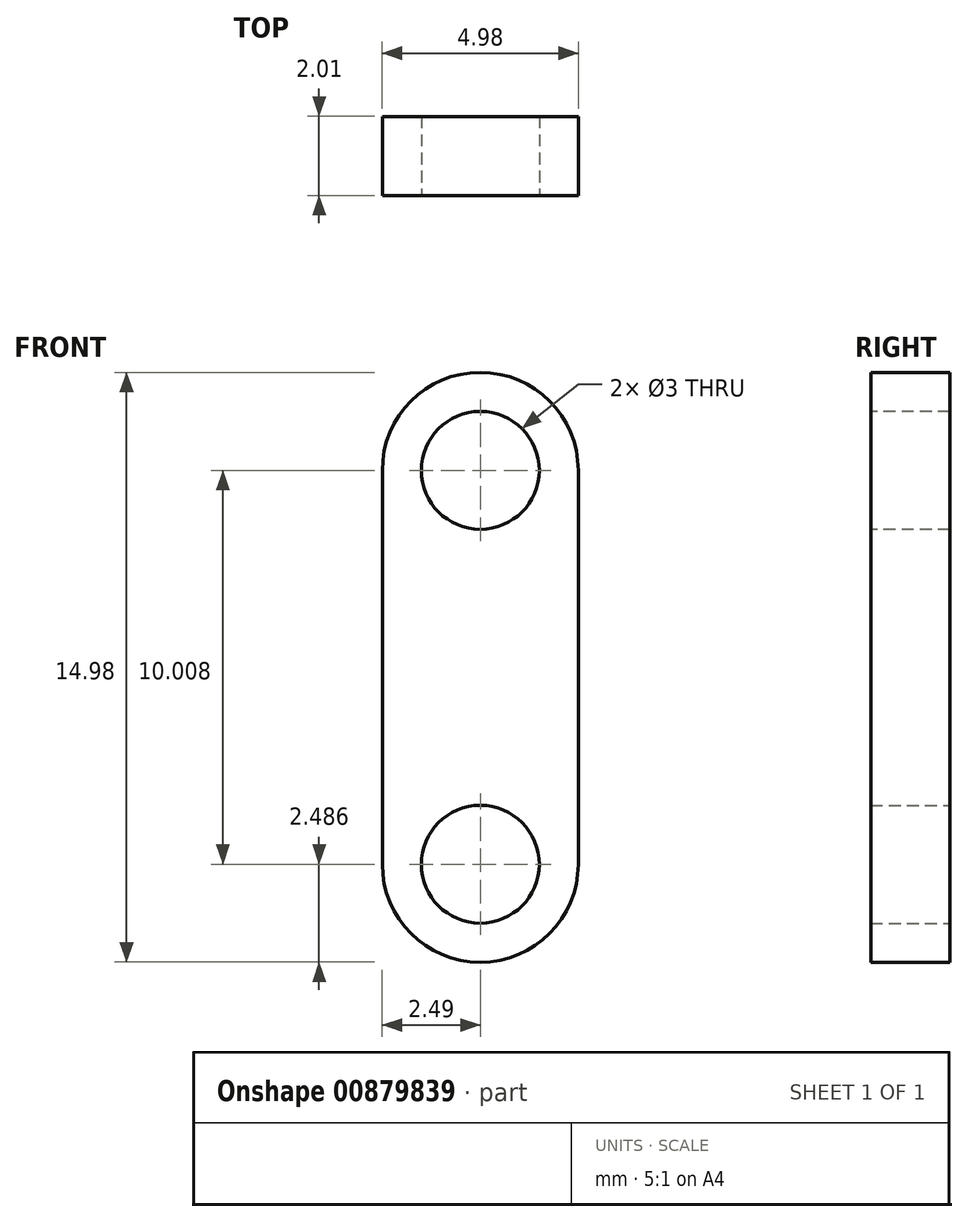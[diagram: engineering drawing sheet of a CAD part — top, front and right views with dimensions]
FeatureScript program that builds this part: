
annotation { "Feature Type Name" : "Feature", "Feature Type Description" : "" }
export const myFeature = defineFeature(function(context is Context, id is Id, definition is map)
    precondition{}
    {
        {
            var Q0;
            Q0=qCreatedBy(makeId("Front.planeOp"),FACE);
            var sketch = newSketch(context, id + "F0", { "sketchPlane" : qUnion([Q0])});
            skLineSegment(sketch, "E0.left", {"start": v(2.49, 5) * mm, "end": v(2.49, -5) * mm});
            skLineSegment(sketch, "E0.right", {"start": v(-2.49, 5) * mm, "end": v(-2.49, -5) * mm});
            skPoint(sketch, "E0.middle", {"position": v(0, 0) * mm});
            skArc(sketch, "E1", {"start": v(2.49, 5) * mm, "mid": v(0, 7.5) * mm, "end": v(-2.49, 5) * mm});
            skArc(sketch, "E2", {"start": v(-2.49, -5) * mm, "mid": v(0, -7.5) * mm, "end": v(2.49, -5) * mm});
            skCircle(sketch, "E3", {"center": v(0, 5) * mm, "radius": 1.5 * mm});
            skSolve(sketch);
        }
        {
            var Q0;
            Q0=makeQuery(id+"F0.imprint","IMPRINT",FACE,{"disambiguationData":[TD([[makeQuery(id+"F0.imprint","IMPRINT",EDGE,{"derivedFrom":sQuery(id+"F0.wireOp",EDGE,"E0.left")}),-1.0]])]});
            extrude(context, id + "F1", {"entities" : qUnion([Q0]), "oppositeDirection" : true, "depth" : 2 * mm, "offsetDistance" : 25.4 * mm});
        }
        {
            var Q0;
            Q0=makeQuery(id+"F1.opExtrude","CAP_FACE",FACE,{"disambiguationData":[OSD([sQuery(id+"F0.wireOp",EDGE,"E0.left"),sQuery(id+"F0.wireOp",EDGE,"E0.right"),sQuery(id+"F0.wireOp",EDGE,"E1"),sQuery(id+"F0.wireOp",EDGE,"E2"),sQuery(id+"F0.wireOp",EDGE,"E3")])],"isStart":false});
            var sketch = newSketch(context, id + "F2", { "sketchPlane" : qUnion([Q0])});
            skCircle(sketch, "E4", {"center": v(0, -5) * mm, "radius": 1.5 * mm});
            skSolve(sketch);
        }
        {
            var Q0;
            Q0=makeQuery(id+"F2.imprint","IMPRINT",FACE,{"disambiguationData":[TD([[makeQuery(id+"F2.imprint","IMPRINT",EDGE,{"derivedFrom":sQuery(id+"F2.wireOp",EDGE,"E4")}),1.0]])]});
            var Q1;
            Q1=sQuery(id+"F2.wireOp",EDGE,"E4");
            extrude(context, id + "F3", {"entities" : qUnion([Q0]), "operationType" : NewBodyOperationType.REMOVE, "surfaceEntities" : qUnion([Q1]), "oppositeDirection" : true, "depth" : 25.4 * mm, "offsetDistance" : 25.4 * mm});
        }
    });
